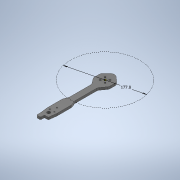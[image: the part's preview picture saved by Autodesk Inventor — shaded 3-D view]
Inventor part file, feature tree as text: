
AUTODESK INVENTOR PART (.ipt)
format: ipt  version: 2020 (Build 240168000, 168)  size: 247,296 bytes
history: native  units: in
note: dims shown in document units (in); Inventor stores cm internally (conversion verified against a paired STEP export)
features: sketch x3, fillet x2, extrude x1, projected_geometry x1
ambient origin geometry x8: Origin, YZ Plane, XZ Plane, XY Plane, X Axis, Y Axis, Z Axis, Center Point
bodies: Solid2 (feature_tree), Solid1 (feature_tree)
feature tree (7):
  sketch  "Sketch1"  dims[d0=7.0in d1=5.72in d2=0.8352in d3=0.2992in]
  sketch  "Sketch2"  dims[d4=0.2992in]
  extrude  "Extrusion1"  Depth=5.72in
  fillet  "Fillet2"  Radius=0.8352in
  fillet  "Fillet3"  Radius=0.2992in
  projected_geometry  "Projected Loop1"
  sketch  "Sketch3"  dims[d5=0.9835in d6=0.9835in d7=0.3937in d8=0.0in d10=0.3937in d11=0.7874in]
